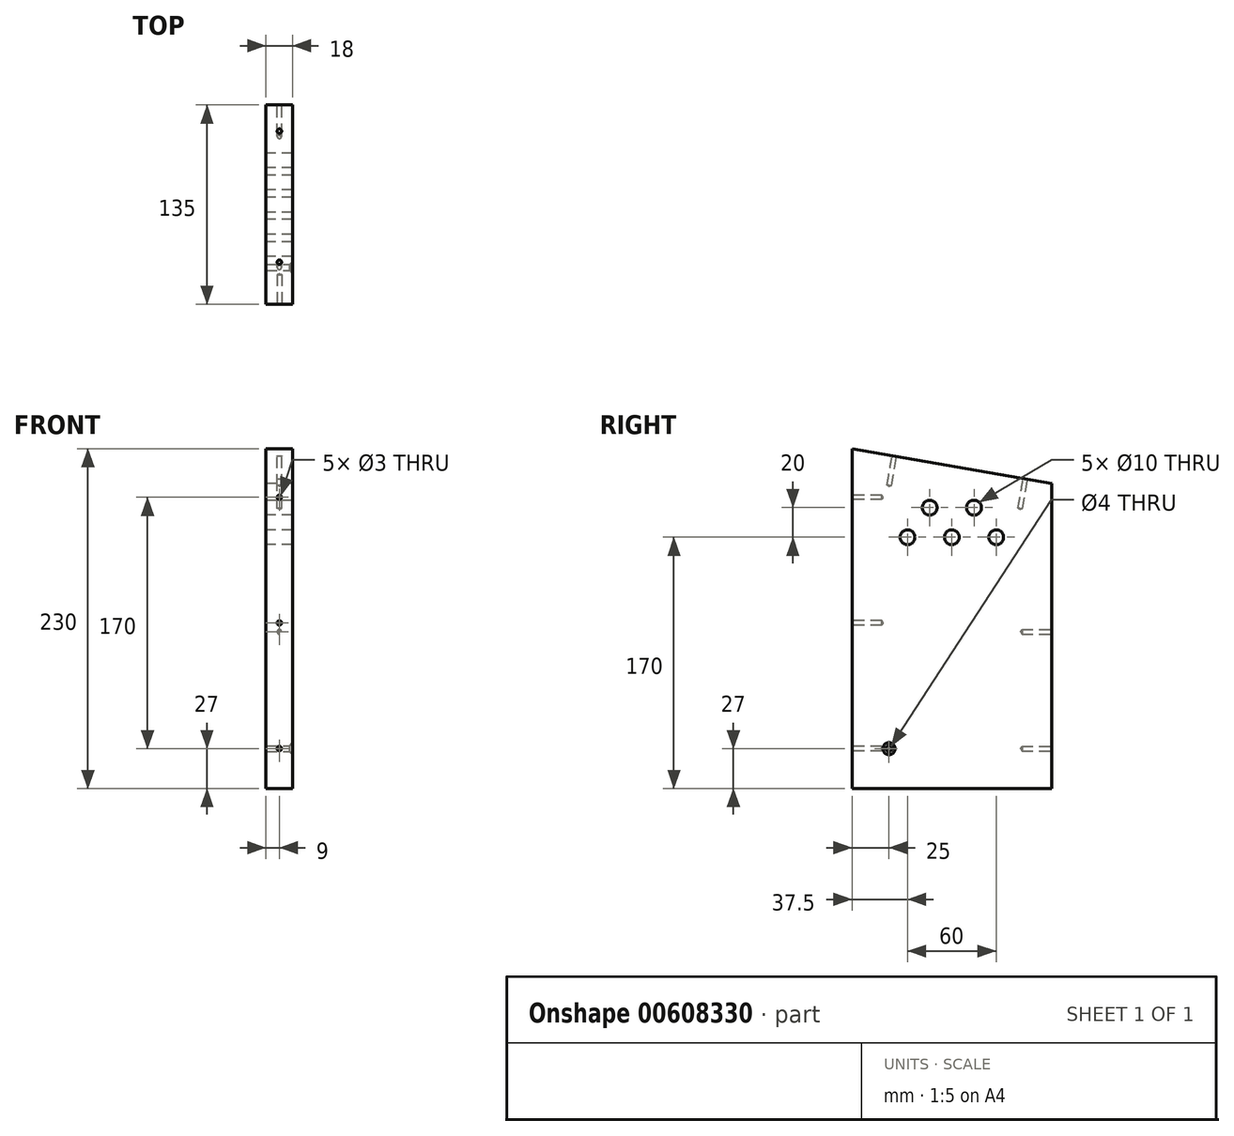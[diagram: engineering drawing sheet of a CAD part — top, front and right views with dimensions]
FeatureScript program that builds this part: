
annotation { "Feature Type Name" : "Feature", "Feature Type Description" : "" }
export const myFeature = defineFeature(function(context is Context, id is Id, definition is map)
    precondition{}
    {
        {
            var Q0;
            Q0=qCreatedBy(makeId("Right.planeOp"),FACE);
            var sketch = newSketch(context, id + "F0", { "sketchPlane" : qUnion([Q0])});
            skLineSegment(sketch, "E0", {"start": v(0, 0) * mm, "end": v(0, 230) * mm});
            skLineSegment(sketch, "E1", {"start": v(0, 230) * mm, "end": v(135, 206.2) * mm});
            skLineSegment(sketch, "E2", {"start": v(135, 206.2) * mm, "end": v(135, 0) * mm});
            skLineSegment(sketch, "E3", {"start": v(135, 0) * mm, "end": v(0, 0) * mm});
            skPoint(sketch, "E4", {"position": v(67.5, 170) * mm});
            skPoint(sketch, "E5", {"position": v(37.5, 170) * mm});
            skPoint(sketch, "E6", {"position": v(97.5, 170) * mm});
            skPoint(sketch, "E7", {"position": v(52.5, 190) * mm});
            skPoint(sketch, "E8", {"position": v(82.5, 190) * mm});
            skPoint(sketch, "E9", {"position": v(67.5, 0) * mm});
            skSolve(sketch);
        }
        {
            var Q0;
            Q0=makeQuery(id+"F0.imprint","IMPRINT",FACE,{"disambiguationData":[TD([[makeQuery(id+"F0.imprint","IMPRINT",EDGE,{"derivedFrom":sQuery(id+"F0.wireOp",EDGE,"E0")}),-1.0]])]});
            extrude(context, id + "F1", {"entities" : qUnion([Q0]), "depth" : 18 * mm, "offsetDistance" : 25 * mm});
        }
        {
            var Q0;
            Q0=sQuery(id+"F0.wireOp",VERTEX,"E5");
            var Q1;
            Q1=sQuery(id+"F0.wireOp",VERTEX,"E4");
            var Q2;
            Q2=sQuery(id+"F0.wireOp",VERTEX,"E6");
            var Q3;
            Q3=makeQuery(id+"F1.opExtrude","SWEPT_BODY",BODY,{"disambiguationData":[OSD([sQuery(id+"F0.wireOp",EDGE,"E0"),sQuery(id+"F0.wireOp",EDGE,"E1"),sQuery(id+"F0.wireOp",EDGE,"E2"),sQuery(id+"F0.wireOp",EDGE,"E3")])]});
            hole(context, id + "F2", {"style" : HoleStyle.SIMPLE, "endStyle" : HoleEndStyle.THROUGH, "oppositeDirection" : true, "holeDiameter" : 10 * mm, "majorDiameter" : 5 * mm, "isTappedThrough" : true, "tappedDepth" : 12 * mm, "tapClearance" : 3, "locations" : qUnion([Q0, Q1, Q2]), "scope" : qUnion([Q3])});
        }
        {
            var Q0;
            Q0=sQuery(id+"F0.wireOp",VERTEX,"E7");
            var Q1;
            Q1=sQuery(id+"F0.wireOp",VERTEX,"E8");
            var Q2;
            Q2=makeQuery(id+"F1.opExtrude","SWEPT_BODY",BODY,{"disambiguationData":[OSD([sQuery(id+"F0.wireOp",EDGE,"E0"),sQuery(id+"F0.wireOp",EDGE,"E1"),sQuery(id+"F0.wireOp",EDGE,"E2"),sQuery(id+"F0.wireOp",EDGE,"E3")])]});
            hole(context, id + "F3", {"style" : HoleStyle.SIMPLE, "endStyle" : HoleEndStyle.THROUGH, "oppositeDirection" : true, "holeDiameter" : 10 * mm, "majorDiameter" : 5 * mm, "isTappedThrough" : true, "tappedDepth" : 12 * mm, "tapClearance" : 3, "locations" : qUnion([Q0, Q1]), "scope" : qUnion([Q2])});
        }
        {
            var Q0;
            Q0=makeQuery(id+"F1.opExtrude","CAP_FACE",FACE,{"disambiguationData":[OSD([sQuery(id+"F0.wireOp",EDGE,"E0"),sQuery(id+"F0.wireOp",EDGE,"E1"),sQuery(id+"F0.wireOp",EDGE,"E2"),sQuery(id+"F0.wireOp",EDGE,"E3")])],"isStart":false});
            var sketch = newSketch(context, id + "F4", { "sketchPlane" : qUnion([Q0])});
            skPoint(sketch, "E10", {"position": v(25, 27) * mm});
            skPoint(sketch, "E11", {"position": v(67.5, 0) * mm});
            skSolve(sketch);
        }
        {
            var Q0;
            Q0=sQuery(id+"F4.wireOp",VERTEX,"E10");
            var Q1;
            Q1=makeQuery(id+"F1.opExtrude","SWEPT_BODY",BODY,{"disambiguationData":[OSD([sQuery(id+"F0.wireOp",EDGE,"E0"),sQuery(id+"F0.wireOp",EDGE,"E1"),sQuery(id+"F0.wireOp",EDGE,"E2"),sQuery(id+"F0.wireOp",EDGE,"E3")])]});
            hole(context, id + "F5", {"style" : HoleStyle.C_SINK, "endStyle" : HoleEndStyle.THROUGH, "holeDiameter" : 4 * mm, "cSinkDiameter" : 8.2 * mm, "cSinkAngle" : 90 * degree, "majorDiameter" : 5 * mm, "isTappedThrough" : true, "tappedDepth" : 12 * mm, "tapClearance" : 3, "locations" : qUnion([Q0]), "scope" : qUnion([Q1])});
        }
        {
            var Q0;
            Q0=makeQuery(id+"F1.opExtrude","SWEPT_FACE",FACE,{"disambiguationData":[OSD([sQuery(id+"F0.wireOp",EDGE,"E2")])]});
            var sketch = newSketch(context, id + "F6", { "sketchPlane" : qUnion([Q0])});
            skPoint(sketch, "E12", {"position": v(-9, 27) * mm});
            skPoint(sketch, "E12.positionSnap0", {"position": v(-9, 0) * mm});
            skPoint(sketch, "E13", {"position": v(-9, 106) * mm});
            skSolve(sketch);
        }
        {
            var Q0;
            Q0=sQuery(id+"F6.wireOp",VERTEX,"E12");
            var Q1;
            Q1=sQuery(id+"F6.wireOp",VERTEX,"E13");
            var Q2;
            Q2=sQuery(id+"F6.wireOp",VERTEX,"8f543f11-4d68-402d-9103-72691adf7820");
            var Q3;
            Q3=makeQuery(id+"F1.opExtrude","SWEPT_BODY",BODY,{"disambiguationData":[OSD([sQuery(id+"F0.wireOp",EDGE,"E0"),sQuery(id+"F0.wireOp",EDGE,"E1"),sQuery(id+"F0.wireOp",EDGE,"E2"),sQuery(id+"F0.wireOp",EDGE,"E3")])]});
            hole(context, id + "F7", {"style" : HoleStyle.SIMPLE, "endStyle" : HoleEndStyle.BLIND, "holeDiameter" : 3 * mm, "majorDiameter" : 5 * mm, "holeDepth" : 20 * mm, "isTappedThrough" : true, "tappedDepth" : 12 * mm, "tapClearance" : 3, "locations" : qUnion([Q0, Q1, Q2]), "scope" : qUnion([Q3])});
        }
        {
            var Q0;
            Q0=makeQuery(id+"F1.opExtrude","SWEPT_FACE",FACE,{"disambiguationData":[OSD([sQuery(id+"F0.wireOp",EDGE,"E0")])]});
            var sketch = newSketch(context, id + "F8", { "sketchPlane" : qUnion([Q0])});
            skPoint(sketch, "E14", {"position": v(9, 27) * mm});
            skPoint(sketch, "E14.positionSnap0", {"position": v(9, 0) * mm});
            skPoint(sketch, "E15", {"position": v(9, 112) * mm});
            skPoint(sketch, "E16", {"position": v(9, 197) * mm});
            skSolve(sketch);
        }
        {
            var Q0;
            Q0=sQuery(id+"F8.wireOp",VERTEX,"E16");
            var Q1;
            Q1=sQuery(id+"F8.wireOp",VERTEX,"E15");
            var Q2;
            Q2=sQuery(id+"F8.wireOp",VERTEX,"E14");
            var Q3;
            Q3=makeQuery(id+"F1.opExtrude","SWEPT_BODY",BODY,{"disambiguationData":[OSD([sQuery(id+"F0.wireOp",EDGE,"E0"),sQuery(id+"F0.wireOp",EDGE,"E1"),sQuery(id+"F0.wireOp",EDGE,"E2"),sQuery(id+"F0.wireOp",EDGE,"E3")])]});
            hole(context, id + "F9", {"style" : HoleStyle.SIMPLE, "endStyle" : HoleEndStyle.BLIND, "holeDiameter" : 3 * mm, "majorDiameter" : 5 * mm, "holeDepth" : 20 * mm, "isTappedThrough" : true, "tappedDepth" : 12 * mm, "tapClearance" : 3, "locations" : qUnion([Q0, Q1, Q2]), "scope" : qUnion([Q3])});
        }
        {
            var Q0;
            Q0=makeQuery(id+"F1.opExtrude","SWEPT_FACE",FACE,{"disambiguationData":[OSD([sQuery(id+"F0.wireOp",EDGE,"E1")])]});
            var sketch = newSketch(context, id + "F10", { "sketchPlane" : qUnion([Q0])});
            skPoint(sketch, "E17", {"position": v(9, 79.14) * mm});
            skPoint(sketch, "E17.positionSnap0", {"position": v(9, 97.14) * mm});
            skPoint(sketch, "E18", {"position": v(9, -10.86) * mm});
            skSolve(sketch);
        }
        {
            var Q0;
            Q0=sQuery(id+"F10.wireOp",VERTEX,"E18");
            var Q1;
            Q1=sQuery(id+"F10.wireOp",VERTEX,"E17");
            var Q2;
            Q2=makeQuery(id+"F1.opExtrude","SWEPT_BODY",BODY,{"disambiguationData":[OSD([sQuery(id+"F0.wireOp",EDGE,"E0"),sQuery(id+"F0.wireOp",EDGE,"E1"),sQuery(id+"F0.wireOp",EDGE,"E2"),sQuery(id+"F0.wireOp",EDGE,"E3")])]});
            hole(context, id + "F11", {"style" : HoleStyle.SIMPLE, "endStyle" : HoleEndStyle.BLIND, "holeDiameter" : 3 * mm, "majorDiameter" : 5 * mm, "holeDepth" : 20 * mm, "isTappedThrough" : true, "tappedDepth" : 12 * mm, "tapClearance" : 3, "locations" : qUnion([Q0, Q1]), "scope" : qUnion([Q2])});
        }
    });
